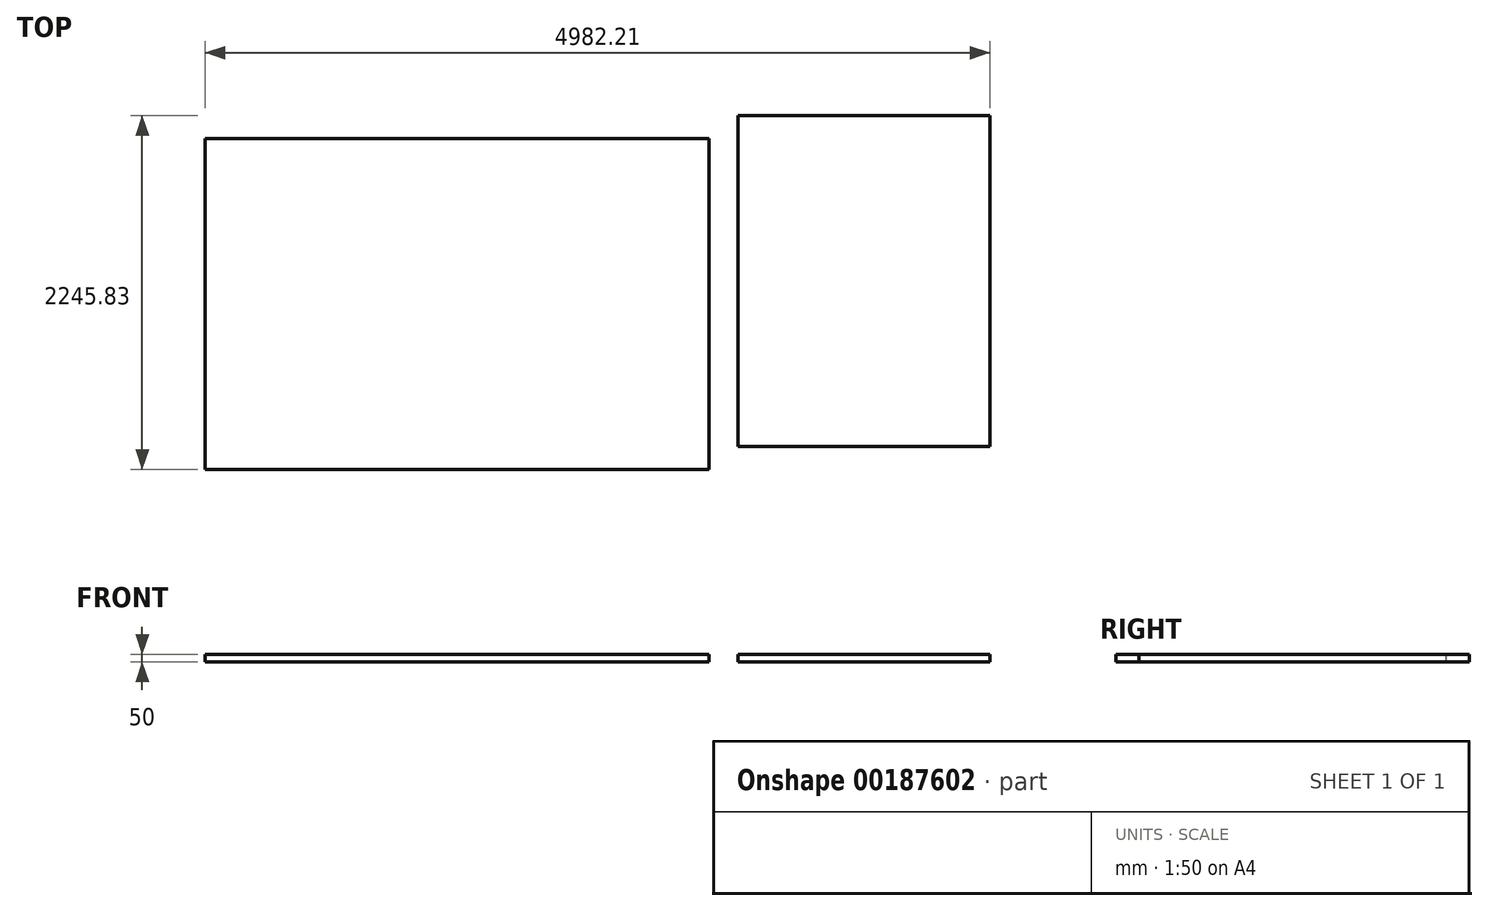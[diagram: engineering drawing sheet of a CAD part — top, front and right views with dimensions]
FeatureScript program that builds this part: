
annotation { "Feature Type Name" : "Feature", "Feature Type Description" : "" }
export const myFeature = defineFeature(function(context is Context, id is Id, definition is map)
    precondition{}
    {
        {
            var Q0;
            Q0=qCreatedBy(makeId("Top.planeOp"),FACE);
            var sketch = newSketch(context, id + "F0", { "sketchPlane" : qUnion([Q0])});
            skLineSegment(sketch, "E0.bottom", {"start": v(-2608.79, 500.53) * mm, "end": v(591.21, 500.53) * mm});
            skLineSegment(sketch, "E0.top", {"start": v(-2608.79, -1599.47) * mm, "end": v(591.21, -1599.47) * mm});
            skLineSegment(sketch, "E0.left", {"start": v(-2608.79, 500.53) * mm, "end": v(-2608.79, -1599.47) * mm});
            skLineSegment(sketch, "E0.right", {"start": v(591.21, 500.53) * mm, "end": v(591.21, -1599.47) * mm});
            skSolve(sketch);
        }
        {
            var Q0;
            Q0=makeQuery(id+"F0.imprint","IMPRINT",FACE,{"disambiguationData":[TD([[makeQuery(id+"F0.imprint","IMPRINT",EDGE,{"derivedFrom":sQuery(id+"F0.wireOp",EDGE,"E0.bottom")}),-1.0]])]});
            extrude(context, id + "F1", {"entities" : qUnion([Q0]), "oppositeDirection" : true, "depth" : 50 * mm});
        }
        {
            var Q0;
            Q0=qCreatedBy(makeId("Top.planeOp"),FACE);
            var sketch = newSketch(context, id + "F2", { "sketchPlane" : qUnion([Q0])});
            skLineSegment(sketch, "E1.bottom", {"start": v(773.42, -1453.64) * mm, "end": v(2373.42, -1453.64) * mm});
            skLineSegment(sketch, "E1.top", {"start": v(773.42, 646.36) * mm, "end": v(2373.42, 646.36) * mm});
            skLineSegment(sketch, "E1.left", {"start": v(773.42, -1453.64) * mm, "end": v(773.42, 646.36) * mm});
            skLineSegment(sketch, "E1.right", {"start": v(2373.42, -1453.64) * mm, "end": v(2373.42, 646.36) * mm});
            skSolve(sketch);
        }
        {
            var Q0;
            Q0=makeQuery(id+"F2.imprint","IMPRINT",FACE,{"disambiguationData":[TD([[makeQuery(id+"F2.imprint","IMPRINT",EDGE,{"derivedFrom":sQuery(id+"F2.wireOp",EDGE,"E1.bottom")}),1.0]])]});
            extrude(context, id + "F3", {"entities" : qUnion([Q0]), "oppositeDirection" : true, "depth" : 50 * mm});
        }
    });
